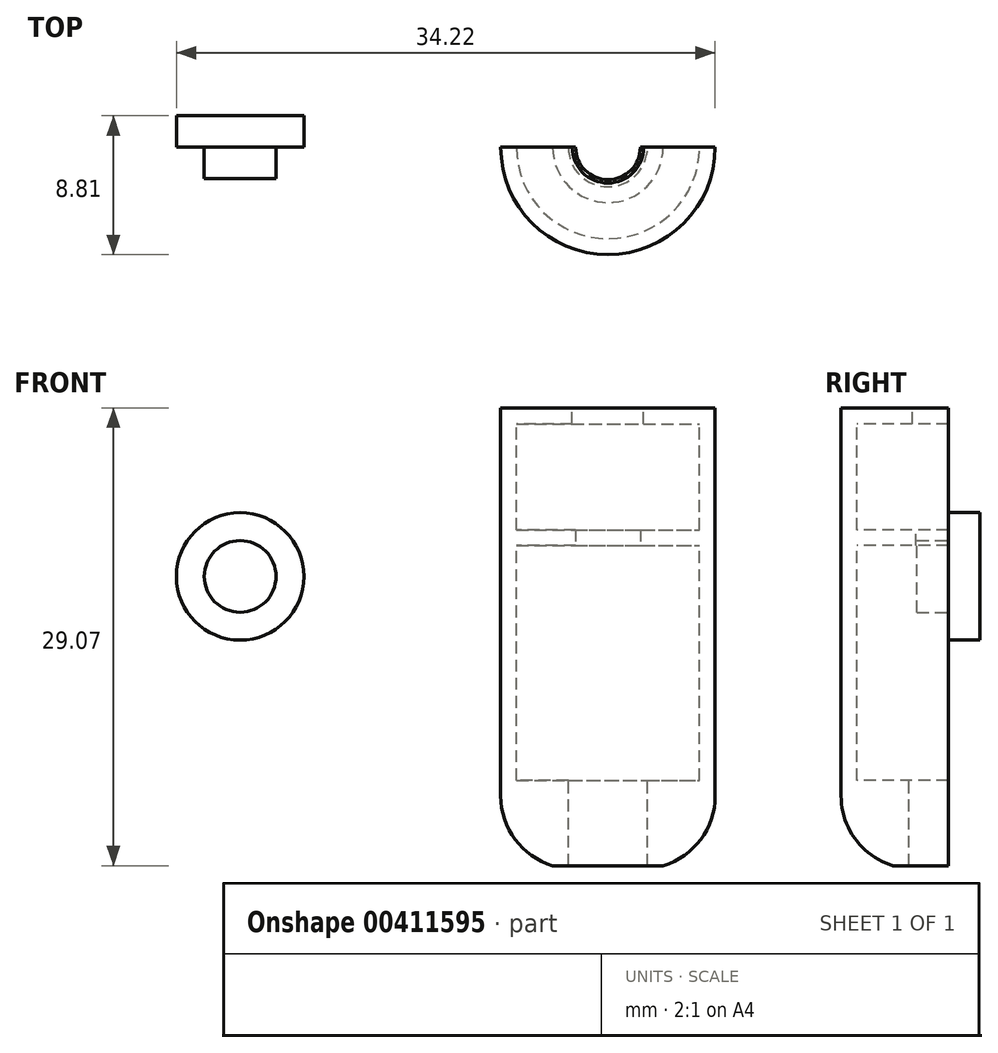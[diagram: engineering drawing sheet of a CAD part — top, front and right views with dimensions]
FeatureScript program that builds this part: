
annotation { "Feature Type Name" : "Feature", "Feature Type Description" : "" }
export const myFeature = defineFeature(function(context is Context, id is Id, definition is map)
    precondition{}
    {
        {
            var Q0;
            Q0=qCreatedBy(makeId("Front.planeOp"),FACE);
            var sketch = newSketch(context, id + "F0", { "sketchPlane" : qUnion([Q0])});
            skLineSegment(sketch, "E0", {"start": v(11.62, 0) * mm, "end": v(11.62, 14.9) * mm});
            skLineSegment(sketch, "E1.1", {"start": v(12.62, -1) * mm, "end": v(12.62, 15.9) * mm});
            skLineSegment(sketch, "E2", {"start": v(8.32, -5.43) * mm, "end": v(8.32, -1) * mm});
            skArc(sketch, "E3", {"start": v(9.32, -5.43) * mm, "mid": v(11.7, -3.76) * mm, "end": v(12.62, -1) * mm});
            skLineSegment(sketch, "E4", {"start": v(8.32, -5.43) * mm, "end": v(9.32, -5.43) * mm});
            skLineSegment(sketch, "E5", {"start": v(8.32, -1) * mm, "end": v(8.32, 0) * mm});
            skLineSegment(sketch, "E6", {"start": v(8.32, 0) * mm, "end": v(11.62, 0) * mm});
            skLineSegment(sketch, "E7", {"start": v(12.62, 19.64) * mm, "end": v(12.62, 15.9) * mm});
            skLineSegment(sketch, "E8", {"start": v(12.62, 19.64) * mm, "end": v(12.62, 20.64) * mm});
            skLineSegment(sketch, "E9", {"start": v(8.08, 19.64) * mm, "end": v(8.08, 20.64) * mm});
            skLineSegment(sketch, "E10", {"start": v(11.62, 15.9) * mm, "end": v(11.62, 19.64) * mm});
            skLineSegment(sketch, "E11", {"start": v(8.08, 19.64) * mm, "end": v(11.62, 19.64) * mm});
            skLineSegment(sketch, "E12", {"start": v(8.08, 20.64) * mm, "end": v(12.62, 20.64) * mm});
            skLineSegment(sketch, "E13", {"start": v(5.81, 20.64) * mm, "end": v(5.81, 14.9) * mm});
            skLineSegment(sketch, "E14", {"start": v(9.72, 15.9) * mm, "end": v(11.62, 15.9) * mm});
            skLineSegment(sketch, "E15", {"start": v(9.72, 14.9) * mm, "end": v(11.62, 14.9) * mm});
            skLineSegment(sketch, "E16.MirrorCS", {"start": v(9.72, 15.9) * mm, "end": v(7.87, 15.9) * mm});
            skLineSegment(sketch, "E17.MirrorCS", {"start": v(7.87, 14.9) * mm, "end": v(9.72, 14.9) * mm});
            skLineSegment(sketch, "E18.MirrorCS", {"start": v(7.87, 15.9) * mm, "end": v(7.87, 14.9) * mm});
            skSolve(sketch);
        }
        {
            var Q0;
            Q0=makeQuery(id+"F0.imprint","IMPRINT",FACE,{"disambiguationData":[TD([[makeQuery(id+"F0.imprint","IMPRINT",EDGE,{"derivedFrom":sQuery(id+"F0.wireOp",EDGE,"E0")}),-1.0]])]});
            var Q1;
            Q1=sQuery(id+"F0.wireOp",EDGE,"E13");
            revolve(context, id + "F1", {"entities" : qUnion([Q0]), "axis" : qUnion([Q1]), "revolveType" : RevolveType.ONE_DIRECTION, "angle" : 180 * degree});
        }
        {
            var Q0;
            Q0=makeQuery(id+"F1.opRevolve","SWEPT_FACE",FACE,{"disambiguationData":[OSD([sQuery(id+"F0.wireOp",EDGE,"E12")])]});
            extrude(context, id + "F2", {"entities" : qUnion([Q0]), "operationType" : NewBodyOperationType.ADD, "depth" : 3 * mm});
        }
        {
            var Q0;
            Q0=makeQuery(id+"F1.opRevolve","SWEPT_FACE",FACE,{"disambiguationData":[OSD([sQuery(id+"F0.wireOp",EDGE,"E11")])]});
            extrude(context, id + "F3", {"entities" : qUnion([Q0]), "operationType" : NewBodyOperationType.REMOVE, "oppositeDirection" : true, "depth" : 3 * mm});
        }
        {
            var Q0;
            Q0=qCreatedBy(makeId("Front.planeOp"),FACE);
            var sketch = newSketch(context, id + "F4", { "sketchPlane" : qUnion([Q0])});
            skCircle(sketch, "E19", {"center": v(-17.55, 12.94) * mm, "radius": 2.28 * mm});
            skCircle(sketch, "E20", {"center": v(-17.55, 12.94) * mm, "radius": 4.07 * mm});
            skSolve(sketch);
        }
        {
            var Q0;
            Q0=makeQuery(id+"F4.imprint","IMPRINT",FACE,{"disambiguationData":[TD([[makeQuery(id+"F4.imprint","IMPRINT",EDGE,{"derivedFrom":sQuery(id+"F4.wireOp",EDGE,"E19")}),1.0]])]});
            extrude(context, id + "F5", {"entities" : qUnion([Q0]), "depth" : 2 * mm});
        }
        {
            var Q0;
            Q0=makeQuery(id+"F5.opExtrude","CAP_FACE",FACE,{"disambiguationData":[OSD([sQuery(id+"F4.wireOp",EDGE,"E19")])],"isStart":true});
            var sketch = newSketch(context, id + "F6", { "sketchPlane" : qUnion([Q0])});
            skCircle(sketch, "E21", {"center": v(17.55, 12.94) * mm, "radius": 4.05 * mm});
            skSolve(sketch);
        }
        {
            var Q0;
            Q0=makeQuery(id+"F6.imprint","IMPRINT",FACE,{"disambiguationData":[TD([[makeQuery(id+"F6.imprint","IMPRINT",EDGE,{"derivedFrom":makeQuery(id+"F5.opExtrude","CAP_EDGE",EDGE,{"disambiguationData":[OSD([sQuery(id+"F4.wireOp",EDGE,"E19")])],"isStart":true})}),-1.0]])]});
            var Q1;
            Q1=makeQuery(id+"F6.imprint","IMPRINT",FACE,{"disambiguationData":[TD([[makeQuery(id+"F6.imprint","IMPRINT",EDGE,{"derivedFrom":sQuery(id+"F6.wireOp",EDGE,"E21")}),1.0]])]});
            extrude(context, id + "F7", {"entities" : qUnion([Q0, Q1]), "operationType" : NewBodyOperationType.ADD, "depth" : 2 * mm});
        }
    });
